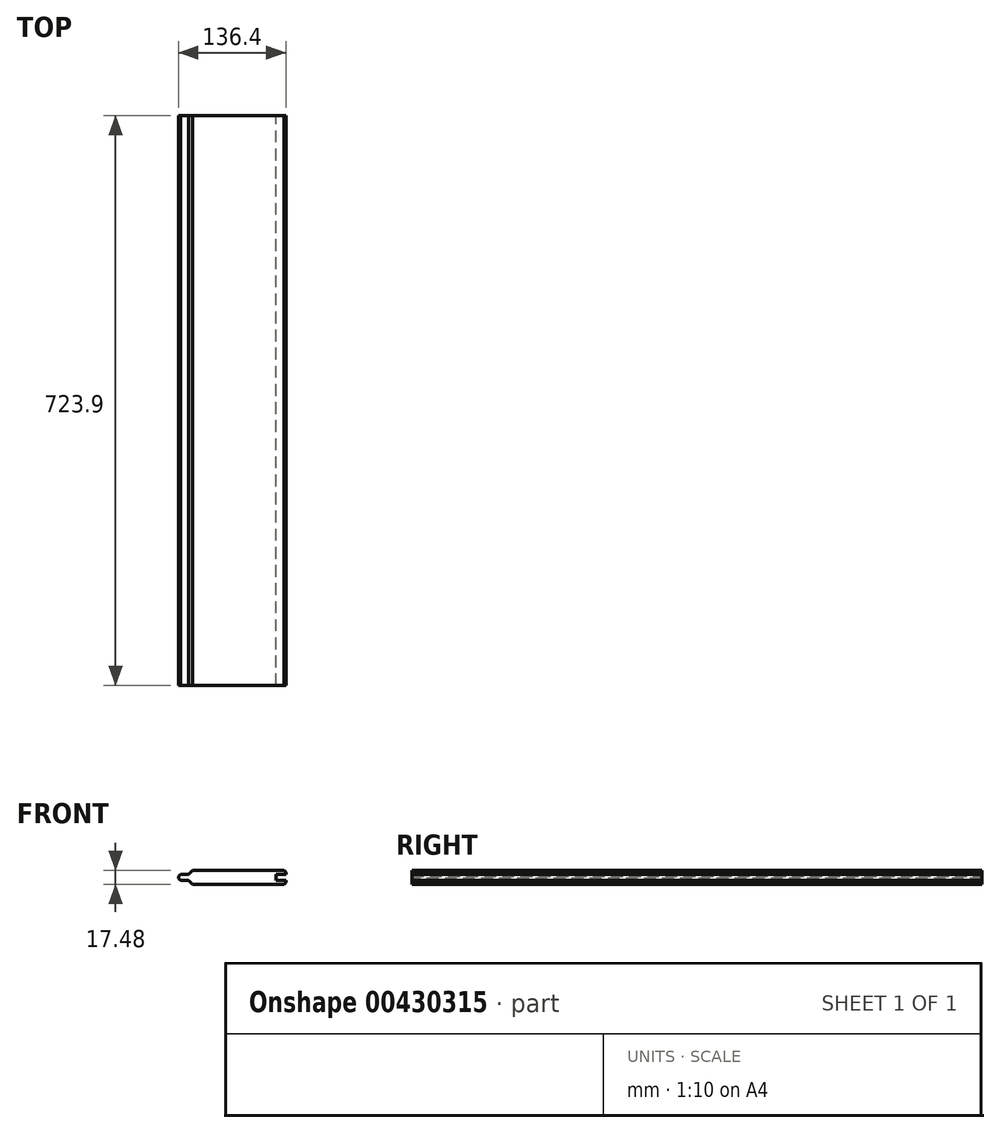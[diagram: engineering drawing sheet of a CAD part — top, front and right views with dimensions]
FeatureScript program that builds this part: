
annotation { "Feature Type Name" : "Feature", "Feature Type Description" : "" }
export const myFeature = defineFeature(function(context is Context, id is Id, definition is map)
    precondition{}
    {
        {
            var Q0;
            Q0=qCreatedBy(makeId("Front.planeOp"),FACE);
            var sketch = newSketch(context, id + "F0", { "sketchPlane" : qUnion([Q0])});
            skLineSegment(sketch, "E0.bottom", {"start": v(68.2, 8.74) * mm, "end": v(-55.5, 8.74) * mm});
            skLineSegment(sketch, "E0.top", {"start": v(68.2, -8.74) * mm, "end": v(-55.5, -8.74) * mm});
            skLineSegment(sketch, "E0.left", {"start": v(68.2, 8.74) * mm, "end": v(68.2, 3.66) * mm});
            skLineSegment(sketch, "E0.right", {"start": v(-68.2, 3.66) * mm, "end": v(-68.2, -3.66) * mm});
            skPoint(sketch, "E0.middle", {"position": v(0, 0) * mm});
            skLineSegment(sketch, "E1.bottom", {"start": v(68.2, 3.66) * mm, "end": v(55.5, 3.66) * mm});
            skLineSegment(sketch, "E1.top", {"start": v(68.2, -3.66) * mm, "end": v(55.5, -3.66) * mm});
            skLineSegment(sketch, "E1.right", {"start": v(55.5, 3.66) * mm, "end": v(55.5, -3.66) * mm});
            skPoint(sketch, "E1.middle", {"position": v(68.2, 0) * mm});
            skPoint(sketch, "E1.left.end.orphan", {"position": v(80.9, -3.66) * mm});
            skPoint(sketch, "E1.left.start.orphan", {"position": v(80.9, 3.66) * mm});
            skLineSegment(sketch, "E2.trimOffspring", {"start": v(68.2, -3.66) * mm, "end": v(68.2, -8.74) * mm});
            skLineSegment(sketch, "E3.bottom", {"start": v(-68.2, 3.66) * mm, "end": v(-55.5, 3.66) * mm});
            skLineSegment(sketch, "E3.right", {"start": v(-55.5, 3.66) * mm, "end": v(-55.5, 8.74) * mm});
            skLineSegment(sketch, "E4.top", {"start": v(-68.2, -3.66) * mm, "end": v(-55.5, -3.66) * mm});
            skLineSegment(sketch, "E4.right", {"start": v(-55.5, -8.74) * mm, "end": v(-55.5, -3.66) * mm});
            skPoint(sketch, "E5.orphan", {"position": v(-68.2, 8.74) * mm});
            skPoint(sketch, "E6.orphan", {"position": v(-68.2, -8.74) * mm});
            skSolve(sketch);
        }
        {
            var Q0;
            Q0=makeQuery(id+"F0.imprint","IMPRINT",FACE,{"disambiguationData":[TD([[makeQuery(id+"F0.imprint","IMPRINT",EDGE,{"derivedFrom":sQuery(id+"F0.wireOp",EDGE,"E0.bottom")}),1.0]])]});
            extrude(context, id + "F1", {"entities" : qUnion([Q0]), "depth" : 723.9 * mm});
        }
        {
            var Q0;
            Q0=makeQuery(id+"F1.opExtrude","SWEPT_EDGE",EDGE,{"disambiguationData":[OSD([sQuery(id+"F0.wireOp",EDGE,"E0.bottom"),sQuery(id+"F0.wireOp",EDGE,"E0.left")])]});
            var Q1;
            Q1=makeQuery(id+"F1.opExtrude","SWEPT_EDGE",EDGE,{"disambiguationData":[OSD([sQuery(id+"F0.wireOp",EDGE,"E0.top"),sQuery(id+"F0.wireOp",EDGE,"E2.trimOffspring")])]});
            var Q2;
            Q2=makeQuery(id+"F1.opExtrude","SWEPT_EDGE",EDGE,{"disambiguationData":[OSD([sQuery(id+"F0.wireOp",EDGE,"E0.right"),sQuery(id+"F0.wireOp",EDGE,"E3.bottom")])]});
            var Q3;
            Q3=makeQuery(id+"F1.opExtrude","SWEPT_EDGE",EDGE,{"disambiguationData":[OSD([sQuery(id+"F0.wireOp",EDGE,"E0.right"),sQuery(id+"F0.wireOp",EDGE,"E4.top")])]});
            chamfer(context, id + "F2", {"entities" : qUnion([Q0, Q1, Q2, Q3]), "width" : 2.54 * mm, "tangentPropagation" : true});
        }
        {
            var Q0;
            Q0=makeQuery(id+"F1.opExtrude","SWEPT_EDGE",EDGE,{"disambiguationData":[OSD([sQuery(id+"F0.wireOp",EDGE,"E0.bottom"),sQuery(id+"F0.wireOp",EDGE,"E3.right")])]});
            var Q1;
            Q1=makeQuery(id+"F1.opExtrude","SWEPT_EDGE",EDGE,{"disambiguationData":[OSD([sQuery(id+"F0.wireOp",EDGE,"E0.top"),sQuery(id+"F0.wireOp",EDGE,"E4.right")])]});
            chamfer(context, id + "F3", {"entities" : qUnion([Q0, Q1]), "width" : 5.08 * mm, "tangentPropagation" : true});
        }
    });
